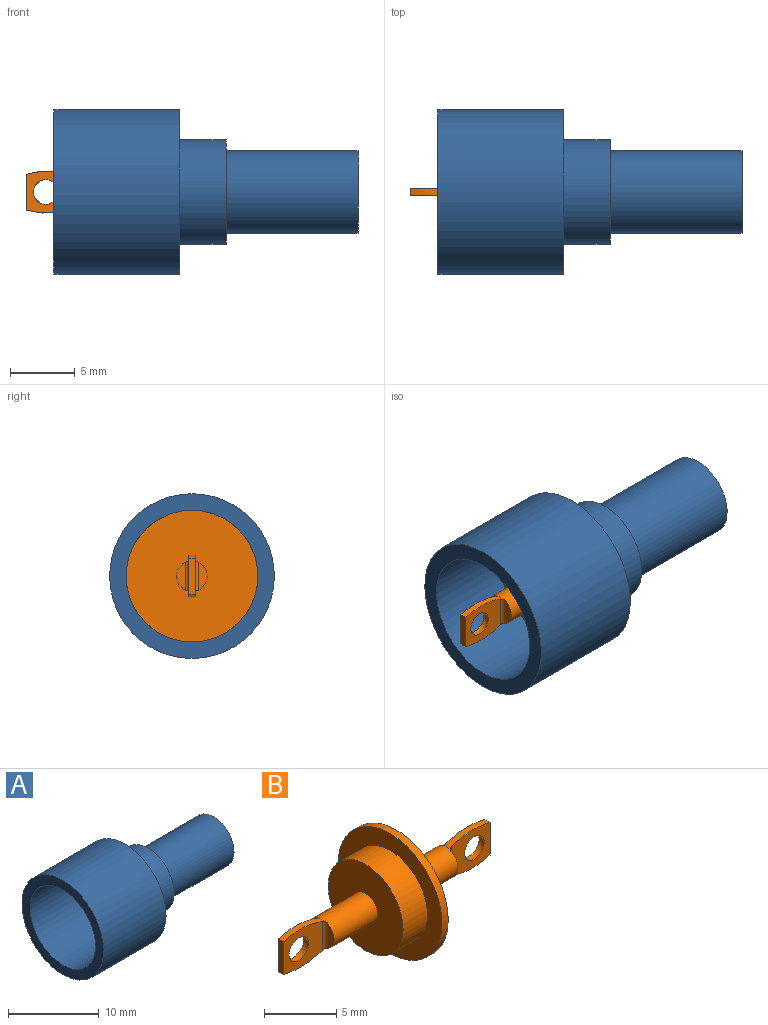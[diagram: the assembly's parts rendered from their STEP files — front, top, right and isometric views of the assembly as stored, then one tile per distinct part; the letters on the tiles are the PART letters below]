
ASSEMBLY  parts=2 mates=1
PART A: 12 faces, bbox 23.5x12.7x12.7 mm
  f0: plane 12.7x12.7mm, normal (1,0,0), area 75.1mm2, adj f1,f11
  f1: cylinder r=6.35mm len=12.7mm, axis (-1,0,0), area 387.6mm2, adj f0,f2
  f2: plane 12.7x12.7mm, normal (-1,0,0), area 45.6mm2, adj f1,f3
  f3: cylinder r=5.08mm len=10.16mm, axis (-1,0,0), area 235.1mm2, adj f2,f4
  f4: plane 10.16x10.16mm, normal (-1,0,0), area 39mm2, adj f3,f5
  f5: cylinder r=3.66mm len=7.32mm, axis (-1,0,0), area 89mm2, adj f4,f6
  f6: plane 7.32x7.32mm, normal (-1,0,0), area 28.5mm2, adj f5,f7
  f7: cylinder r=2.07mm len=12.22mm, axis (-1,0,0), area 159.1mm2, adj f6,f8
  f8: plane 6.35x6.35mm, normal (1,0,0), area 18.2mm2, adj f7,f9
  f9: cylinder r=3.17mm len=10.18mm, axis (-1,0,0), area 203.1mm2, adj f8,f10
  f10: plane 8.1x8.1mm, normal (1,0,0), area 19.9mm2, adj f9,f11
  f11: cylinder r=4.05mm len=8.1mm, axis (-1,0,0), area 90.7mm2, adj f0,f10
PART B: 27 faces, bbox 20.3x10.2x10.2 mm
  f0: revolved ~3.97x0.86mm, area 2.1mm2, adj f10,f12,f18,f21,f25,f26
  f1: plane 2.79x0.51mm, normal (1,0,0), area 1.4mm2, adj f2,f3,f13,f16
  f2: revolved ~3.97x0.86mm, area 2.1mm2, adj f1,f4,f13,f16,f23,f24
  f3: revolved ~3.97x0.86mm, area 2.1mm2, adj f1,f4,f13,f16,f23,f24
  f4: cylinder r=1.18mm len=4.95mm, axis (-1,0,0), area 36.2mm2, adj f2,f3,f5,f14,f15,f23,f24
  f5: plane 10.16x10.16mm, normal (1,0,0), area 76.7mm2, adj f4,f6
  f6: cylinder r=5.08mm len=10.16mm, axis (-1,0,0), area 19.5mm2, adj f5,f7
  f7: plane 10.16x10.16mm, normal (-1,0,0), area 39mm2, adj f6,f8
  f8: cylinder r=3.66mm len=7.32mm, axis (-1,0,0), area 54.9mm2, adj f7,f9
  f9: plane 7.32x7.32mm, normal (-1,0,0), area 37.6mm2, adj f8,f10
  f10: cylinder r=1.18mm len=4.36mm, axis (-1,0,0), area 31.8mm2, adj f0,f9,f11,f19,f20,f25,f26
  f11: revolved ~3.97x0.86mm, area 2.1mm2, adj f10,f12,f18,f21,f25,f26
  f12: plane 2.79x0.51mm, normal (-1,0,0), area 1.4mm2, adj f0,f11,f18,f21
  f13: plane 3.82x3.23mm, normal (0,1,0), area 8.6mm2, adj f1,f2,f3,f17,f23
  f14: plane 2.13x0.67mm, normal (1,0,0), area 1mm2, adj f4,f23
  f15: plane 2.13x0.67mm, normal (1,0,0), area 1mm2, adj f4,f24
  f16: plane 3.82x3.23mm, normal (0,-1,0), area 8.6mm2, adj f1,f2,f3,f17,f24
  f17: sphere r=0.99mm, area 3.2mm2, adj f13,f16
  f18: plane 3.82x3.23mm, normal (0,1,0), area 8.6mm2, adj f0,f11,f12,f22,f26
  f19: plane 2.13x0.67mm, normal (-1,0,0), area 1mm2, adj f10,f26
  f20: plane 2.13x0.67mm, normal (-1,0,0), area 1mm2, adj f10,f25
  f21: plane 3.82x3.23mm, normal (0,-1,0), area 8.6mm2, adj f0,f11,f12,f22,f25
  f22: sphere r=0.99mm, area 3.2mm2, adj f18,f21
  f23: cylinder r=0.25mm len=2.43mm, axis (0,0,-1), area 0.9mm2, adj f2,f3,f4,f13,f14
  f24: cylinder r=0.25mm len=2.43mm, axis (0,0,1), area 0.9mm2, adj f2,f3,f4,f15,f16
  f25: cylinder r=0.25mm len=2.43mm, axis (0,0,-1), area 0.9mm2, adj f0,f10,f11,f20,f21
  f26: cylinder r=0.25mm len=2.43mm, axis (0,0,1), area 0.9mm2, adj f0,f10,f11,f18,f19
PLACE A at identity fixed
PLACE B rot(axis=(0,1,0),180deg) t=(0.6,0,0)mm
MATE fastened B.f4 <-> A.f1  axis (1,0,0) through (0,0,0)mm
